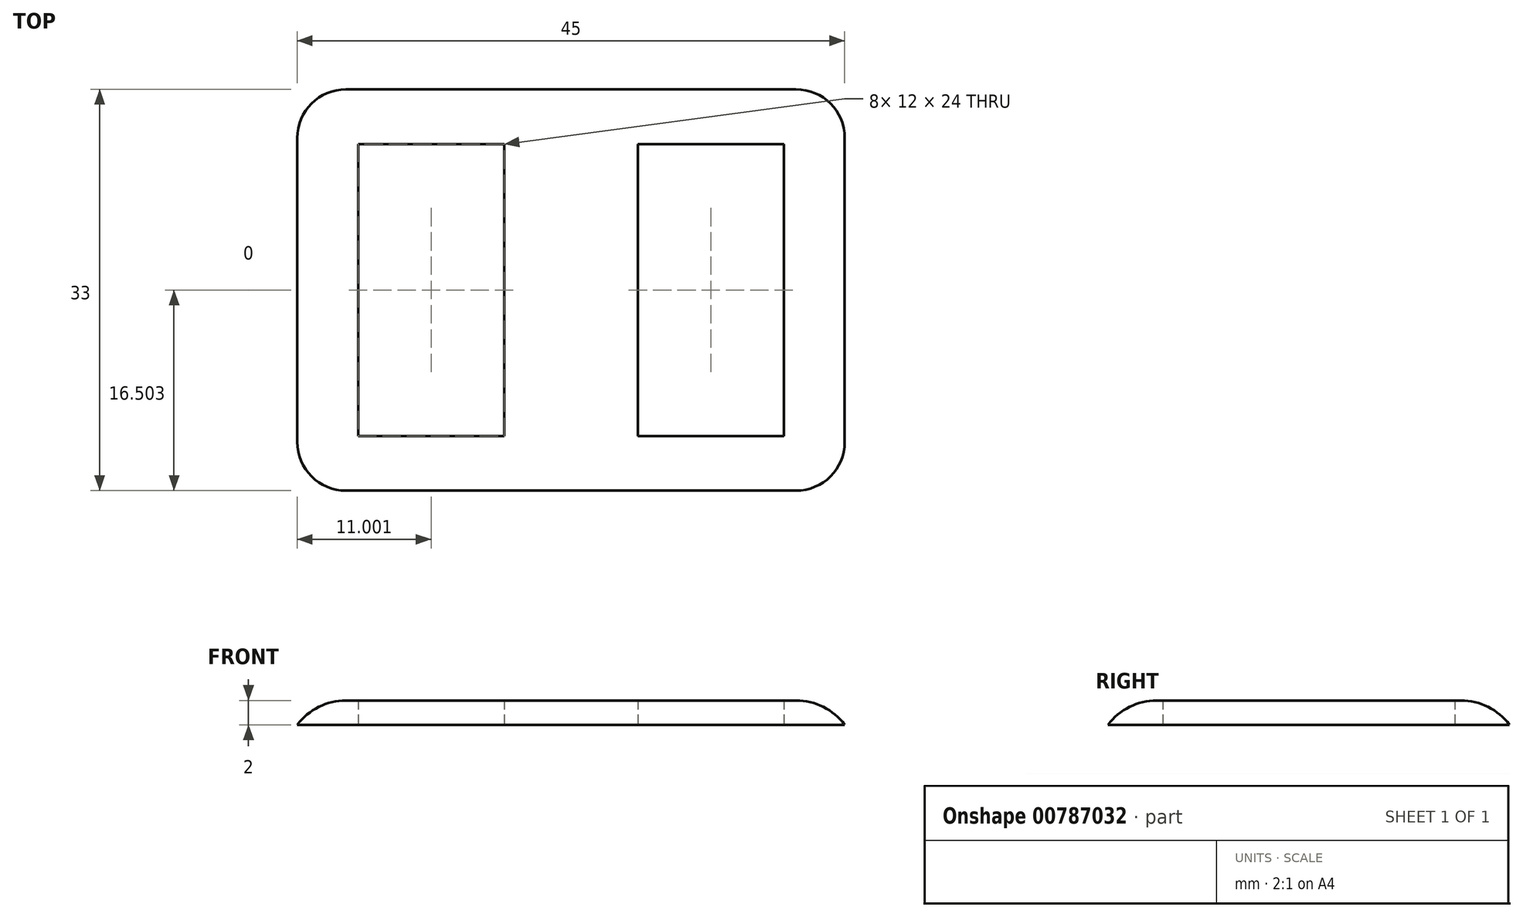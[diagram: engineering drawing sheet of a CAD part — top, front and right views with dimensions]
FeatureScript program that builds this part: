
annotation { "Feature Type Name" : "Feature", "Feature Type Description" : "" }
export const myFeature = defineFeature(function(context is Context, id is Id, definition is map)
    precondition{}
    {
        {
            var Q0;
            Q0=qCreatedBy(makeId("Top.planeOp"),FACE);
            var sketch = newSketch(context, id + "F0", { "sketchPlane" : qUnion([Q0])});
            skLineSegment(sketch, "E0.bottom", {"start": v(-29.74, 7.56) * mm, "end": v(15.26, 7.56) * mm});
            skLineSegment(sketch, "E0.top", {"start": v(-29.74, -27.44) * mm, "end": v(15.26, -27.44) * mm});
            skLineSegment(sketch, "E0.left", {"start": v(-29.74, 7.56) * mm, "end": v(-29.74, -27.44) * mm});
            skLineSegment(sketch, "E0.right", {"start": v(15.26, 7.56) * mm, "end": v(15.26, -27.44) * mm});
            skSolve(sketch);
        }
        {
            var Q0;
            Q0=makeQuery(id+"F0.imprint","IMPRINT",FACE,{"disambiguationData":[TD([[makeQuery(id+"F0.imprint","IMPRINT",EDGE,{"derivedFrom":sQuery(id+"F0.wireOp",EDGE,"E0.bottom")}),-1.0]])]});
            var sketch = newSketch(context, id + "F1", { "sketchPlane" : qUnion([Q0])});
            skLineSegment(sketch, "E1.bottom", {"start": v(-24.74, 2.06) * mm, "end": v(-12.74, 2.06) * mm});
            skLineSegment(sketch, "E1.top", {"start": v(-24.74, -21.94) * mm, "end": v(-12.74, -21.94) * mm});
            skLineSegment(sketch, "E1.left", {"start": v(-24.74, 2.06) * mm, "end": v(-24.74, -21.94) * mm});
            skLineSegment(sketch, "E1.right", {"start": v(-12.74, 2.06) * mm, "end": v(-12.74, -21.94) * mm});
            skLineSegment(sketch, "E2.bottom", {"start": v(-1.74, 2.06) * mm, "end": v(10.26, 2.06) * mm});
            skLineSegment(sketch, "E2.top", {"start": v(-1.74, -21.94) * mm, "end": v(10.26, -21.94) * mm});
            skLineSegment(sketch, "E2.left", {"start": v(-1.74, 2.06) * mm, "end": v(-1.74, -21.94) * mm});
            skLineSegment(sketch, "E2.right", {"start": v(10.26, 2.06) * mm, "end": v(10.26, -21.94) * mm});
            skSolve(sketch);
        }
        {
            var Q0;
            Q0=makeQuery(id+"F1.imprint","IMPRINT",FACE,{"disambiguationData":[TD([[makeQuery(id+"F1.imprint","IMPRINT",EDGE,{"derivedFrom":sQuery(id+"F1.wireOp",EDGE,"E1.bottom")}),1.0]])]});
            extrude(context, id + "F2", {"entities" : qUnion([Q0]), "depth" : 2 * mm, "offsetDistance" : 25 * mm});
        }
        {
            var Q0;
            Q0=makeQuery(id+"F2.opExtrude","CAP_EDGE",EDGE,{"disambiguationData":[OSD([sQuery(id+"F0.wireOp",EDGE,"E0.left")])],"isStart":false});
            fillet(context, id + "F3", {"entities" : qUnion([Q0]), "radius" : 5 * mm, "tangentPropagation" : true, "allowEdgeOverflow" : false});
        }
        {
            var Q0;
            Q0=makeQuery(id+"F2.opExtrude","CAP_EDGE",EDGE,{"disambiguationData":[OSD([sQuery(id+"F0.wireOp",EDGE,"E0.right")])],"isStart":false});
            fillet(context, id + "F4", {"entities" : qUnion([Q0]), "radius" : 5 * mm, "tangentPropagation" : true, "allowEdgeOverflow" : false});
        }
        {
            var Q0;
            Q0=makeQuery(id+"F2.opExtrude","CAP_EDGE",EDGE,{"disambiguationData":[OSD([sQuery(id+"F0.wireOp",EDGE,"E0.top")])],"isStart":false});
            fillet(context, id + "F5", {"entities" : qUnion([Q0]), "radius" : 5 * mm, "tangentPropagation" : true, "allowEdgeOverflow" : false});
        }
        {
            var Q0;
            Q0=makeQuery(id+"F2.opExtrude","CAP_EDGE",EDGE,{"disambiguationData":[OSD([sQuery(id+"F0.wireOp",EDGE,"E0.bottom")])],"isStart":false});
            fillet(context, id + "F6", {"entities" : qUnion([Q0]), "radius" : 5 * mm, "tangentPropagation" : true, "allowEdgeOverflow" : false});
        }
    });
